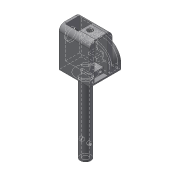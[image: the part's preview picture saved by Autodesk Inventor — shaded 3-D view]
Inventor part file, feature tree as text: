
AUTODESK INVENTOR PART (.ipt)
format: ipt  version: 2018 (Build 220112000, 112)  size: 359,936 bytes
history: native  units: mm
features: sketch x14, extrude x13, other x10, fillet x3
ambient origin geometry x8: Origin, YZ Plane, XZ Plane, XY Plane, X Axis, Y Axis, Z Axis, Center Point
bodies: Solid1 (feature_tree)
feature tree (40):
  extrude  "base"  Depth=20.0mm
  extrude  "attacher"  Depth=10.0mm
  fillet  "Fillet2"  Radius=9.5mm
  extrude  "hole_bar_rigify"  Depth=4.0mm
  extrude  "servo_place"  Depth=12.0mm TaperAngle=0.0deg
  extrude  "servo_place_2"  Depth=11.6mm
  fillet  "Fillet3"  Radius=12.5mm
  extrude  "rot_axis"  Depth=23.0mm TaperAngle=0.0deg
  extrude  "cable_hole"  Depth=4.7mm
  fillet  "Fillet5"  Radius=6.6mm
  extrude  "cable_guide_1"  Depth=5.0mm
  sketch  "Sketch23"  dims[d94=12.0mm d95=10.0mm]
  sketch  "Sketch24"  dims[d96=8.0mm d97=0.0mm d105=6.0mm]
  extrude  "cable_guide_2"  Depth=10.0mm
  extrude  "cable_guide_3"  Depth=6.0mm
  other  "cable_guide_4"
  extrude  "Extrusion25"  Depth=6.0mm
  other  "Edición directa1"
  other  "Edición directa2"
  other  "Edición directa3"
  other  "Edición directa4"
  extrude  "Extrusión26"  Depth=5.0mm
  extrude  "Extrusión27"  Depth=5.0mm
  sketch  "Sketch1"  dims[d0=25.0mm d1=20.0mm]
  sketch  "Sketch4"  dims[d2=35.0mm d3=0.0mm d18=10.0mm d19=9.5mm]
  sketch  "Sketch5"  dims[d20=100.0mm d21=0.0mm d22=4.0mm]
  sketch  "Sketch15"  dims[d23=5.0mm d24=12.0mm d25=0.0mm]
  sketch  "Sketch16"  dims[d76=6.25mm d77=11.6mm d78=12.5mm]
  sketch  "Sketch18"  dims[d79=23.2mm d80=23.0mm d81=0.0mm]
  sketch  "Sketch21"  dims[d82=4.7mm d83=4.7mm d84=6.6mm d85=0.0mm]
  sketch  "Sketch22"  dims[d92=20.0mm d93=5.0mm]
  sketch  "Sketch25"  dims[d106=10.0mm d107=0.0mm d108=6.0mm]
  sketch  "Sketch26"  dims[d109=10.0mm d110=5.0mm]
  sketch  "Boceto27"  dims[d111=5.0mm d112=5.0mm]
  sketch  "Boceto28"  dims[d113=5.0mm d114=15.0mm d115=15.0mm d116=5.0mm d117=15.0mm d118=8.0mm d119=0.0mm d120=2.0mm d121=11.0mm d122=7.0mm d123=2.0mm d124=11.0mm d125=7.0mm d126=8.0mm d127=0.0mm d128=8.0mm d129=0.0mm d130=90.0deg d131=13.0mm d132=3.0mm d133=10.0mm d134=0.0mm d135=0.0mm d136=0.0mm d137=-33.0mm d138=0.0mm d139=0.0mm d140=5.6mm d141=0.0mm d142=0.0mm d143=-2.6mm d144=-4.1mm d145=0.0mm d146=0.0mm d147=0.0mm d148=0.0mm d149=4.0mm d150=2.5mm d151=2.5mm d152=2.5mm d153=10.0mm d154=0.0mm d157=10.0mm d158=0.0mm]
  other  "Desplazar1"
  other  "Desplazar2"
  other  "Desplazar3"
  other  "Desplazar4"
  other  "Desplazar5"
